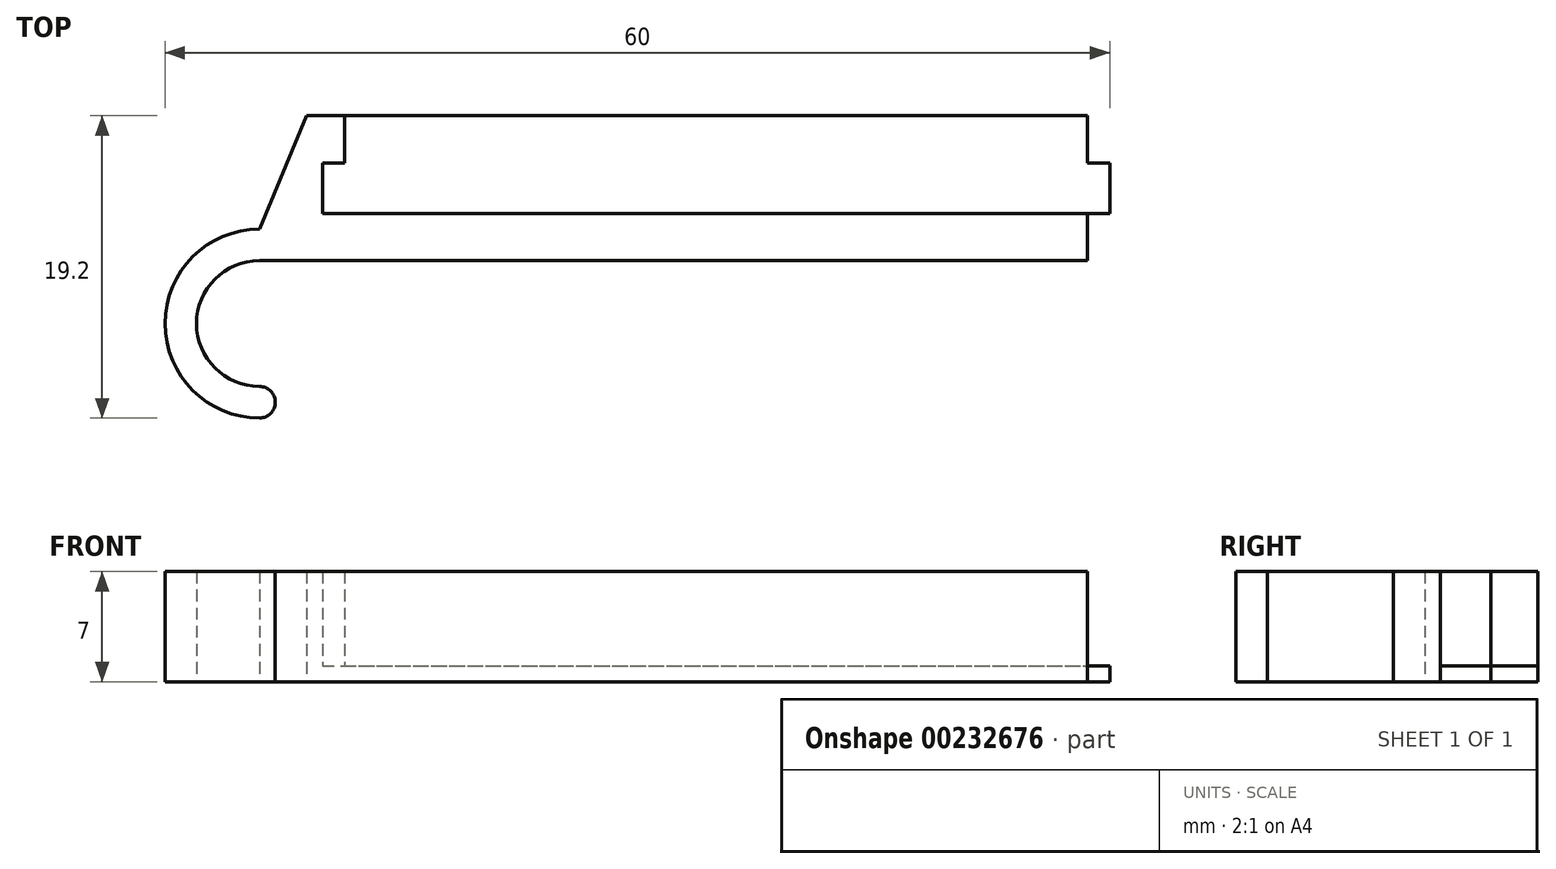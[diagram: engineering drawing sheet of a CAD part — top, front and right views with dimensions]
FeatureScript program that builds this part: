
annotation { "Feature Type Name" : "Feature", "Feature Type Description" : "" }
export const myFeature = defineFeature(function(context is Context, id is Id, definition is map)
    precondition{}
    {
        {
            var Q0;
            Q0=qCreatedBy(makeId("Top.planeOp"),FACE);
            var sketch = newSketch(context, id + "F0", { "sketchPlane" : qUnion([Q0])});
            skLineSegment(sketch, "E0", {"start": v(0, 5.73) * mm, "end": v(-29, 5.73) * mm});
            skArc(sketch, "E1", {"start": v(-29, 5.73) * mm, "mid": v(-33, 1.73) * mm, "end": v(-29, -2.27) * mm});
            skArc(sketch, "E2", {"start": v(-29, 7.73) * mm, "mid": v(-35, 1.73) * mm, "end": v(-29, -4.27) * mm});
            skLineSegment(sketch, "E3", {"start": v(-25, 8.73) * mm, "end": v(0, 8.73) * mm});
            skArc(sketch, "E4", {"start": v(-29, -4.27) * mm, "mid": v(-28, -3.27) * mm, "end": v(-29, -2.27) * mm});
            skLineSegment(sketch, "E5", {"start": v(0, -8.32) * mm, "end": v(0, 17.12) * mm, "construction": true});
            skLineSegment(sketch, "E6.MirrorCS", {"start": v(0, 5.73) * mm, "end": v(29, 5.73) * mm});
            skLineSegment(sketch, "E7.MirrorCS", {"start": v(25, 8.73) * mm, "end": v(0, 8.73) * mm});
            skArc(sketch, "E8.MirrorCS", {"start": v(29, 5.73) * mm, "mid": v(33, 1.73) * mm, "end": v(29, -2.27) * mm});
            skArc(sketch, "E9.MirrorCS", {"start": v(29, -4.27) * mm, "mid": v(28, -3.27) * mm, "end": v(29, -2.27) * mm});
            skArc(sketch, "E10.MirrorCS", {"start": v(29, 7.73) * mm, "mid": v(35, 1.73) * mm, "end": v(29, -4.27) * mm});
            skCircle(sketch, "E11", {"center": v(-29, 1.73) * mm, "radius": 4 * mm, "construction": true});
            skLineSegment(sketch, "E12", {"start": v(-29, 7.73) * mm, "end": v(-26, 14.93) * mm});
            skLineSegment(sketch, "E13", {"start": v(-26, 14.93) * mm, "end": v(0, 14.93) * mm});
            skLineSegment(sketch, "E14.MirrorCS", {"start": v(29, 7.73) * mm, "end": v(26, 14.93) * mm});
            skLineSegment(sketch, "E15.MirrorCS", {"start": v(26, 14.93) * mm, "end": v(0, 14.93) * mm});
            skLineSegment(sketch, "E16", {"start": v(-23.6, 5.73) * mm, "end": v(-23.6, 8.73) * mm});
            skLineSegment(sketch, "E17", {"start": v(-25, 8.73) * mm, "end": v(-25, 11.93) * mm});
            skLineSegment(sketch, "E18", {"start": v(-25, 11.93) * mm, "end": v(0, 11.93) * mm});
            skLineSegment(sketch, "E19.MirrorCS", {"start": v(23.6, 5.73) * mm, "end": v(23.6, 8.73) * mm});
            skLineSegment(sketch, "E20.MirrorCS", {"start": v(25, 8.73) * mm, "end": v(25, 11.93) * mm});
            skLineSegment(sketch, "E21.MirrorCS", {"start": v(25, 11.93) * mm, "end": v(0, 11.93) * mm});
            skLineSegment(sketch, "E22", {"start": v(-29, 1.73) * mm, "end": v(-29, -4.27) * mm, "construction": true});
            skLineSegment(sketch, "E23", {"start": v(-23.6, 11.93) * mm, "end": v(-23.6, 14.93) * mm});
            skLineSegment(sketch, "E24.MirrorCS", {"start": v(23.6, 11.93) * mm, "end": v(23.6, 14.93) * mm});
            skSolve(sketch);
        }
        {
            var Q0;
            {var subQ0=sQuery(id+"F0.wireOp",EDGE,"E8.MirrorCS");Q0=makeQuery(id+"F0.imprint","IMPRINT",FACE,{"disambiguationData":[TD([[makeQuery(id+"F0.imprint","IMPRINT",EDGE,{"derivedFrom":subQ0}),1.0]])]});}
            var Q1;
            {var subQ3=sQuery(id+"F0.wireOp",EDGE,"E1");Q1=makeQuery(id+"F0.imprint","IMPRINT",FACE,{"disambiguationData":[TD([[makeQuery(id+"F0.imprint","IMPRINT",EDGE,{"derivedFrom":subQ3}),-1.0]])]});}
            var Q2;
            {var subQ1=sQuery(id+"F0.wireOp",EDGE,"E12");Q2=makeQuery(id+"F0.imprint","IMPRINT",FACE,{"disambiguationData":[TD([[makeQuery(id+"F0.imprint","IMPRINT",EDGE,{"derivedFrom":subQ1}),-1.0]])]});}
            var Q3;
            {var subQ7=sQuery(id+"F0.wireOp",EDGE,"E16");Q3=makeQuery(id+"F0.imprint","IMPRINT",FACE,{"disambiguationData":[TD([[makeQuery(id+"F0.imprint","IMPRINT",EDGE,{"derivedFrom":subQ7}),-1.0]])]});}
            extrude(context, id + "F1", {"entities" : qUnion([Q0, Q1, Q2, Q3]), "depth" : 7 * mm});
        }
        {
            var Q0;
            {var subQ6=sQuery(id+"F0.wireOp",EDGE,"E17");Q0=makeQuery(id+"F0.imprint","IMPRINT",FACE,{"disambiguationData":[TD([[makeQuery(id+"F0.imprint","IMPRINT",EDGE,{"derivedFrom":subQ6}),-1.0]])]});}
            var Q1;
            {var subQ7=sQuery(id+"F0.wireOp",EDGE,"E23");Q1=makeQuery(id+"F0.imprint","IMPRINT",FACE,{"disambiguationData":[TD([[makeQuery(id+"F0.imprint","IMPRINT",EDGE,{"derivedFrom":subQ7}),-1.0]])]});}
            extrude(context, id + "F2", {"entities" : qUnion([Q0, Q1]), "operationType" : NewBodyOperationType.ADD, "depth" : 1 * mm});
        }
    });
